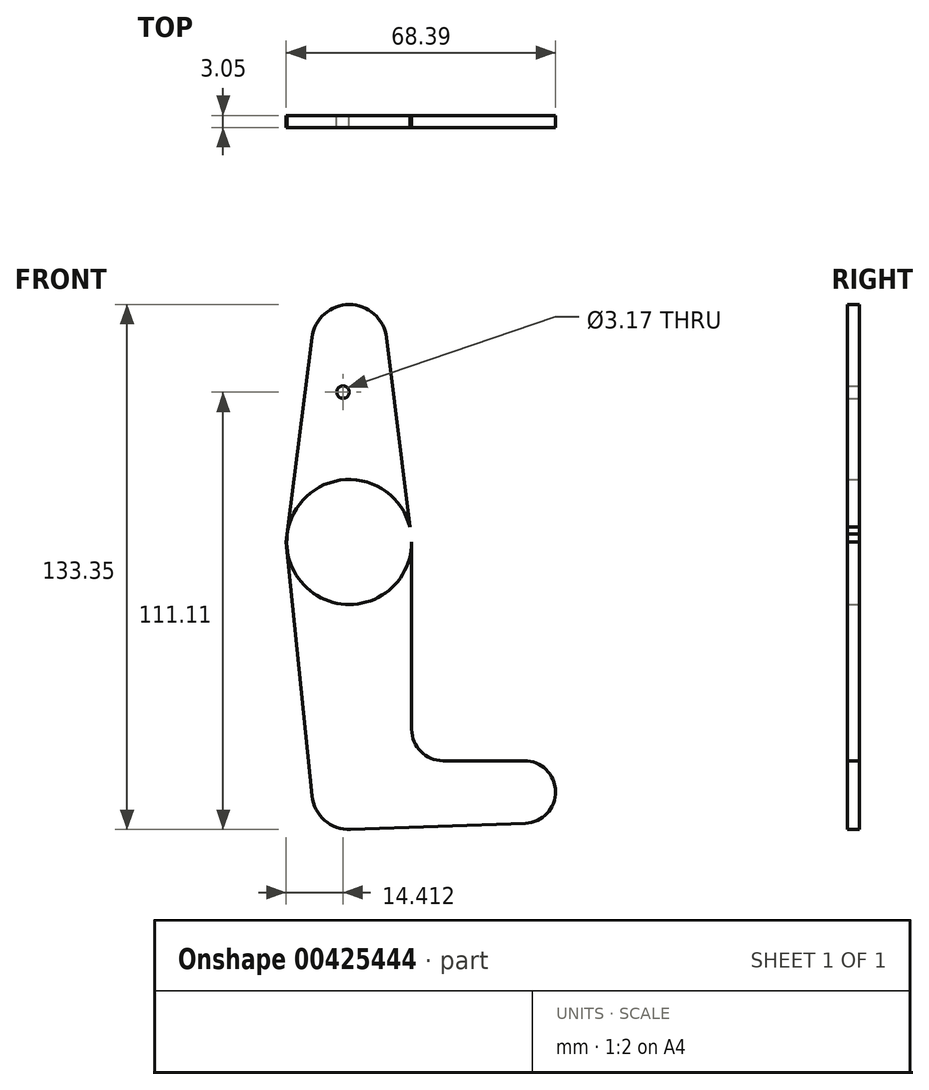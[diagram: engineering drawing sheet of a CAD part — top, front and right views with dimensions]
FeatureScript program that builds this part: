
annotation { "Feature Type Name" : "Feature", "Feature Type Description" : "" }
export const myFeature = defineFeature(function(context is Context, id is Id, definition is map)
    precondition{}
    {
        {
            var Q0;
            Q0=qCreatedBy(makeId("Front.planeOp"),FACE);
            var sketch = newSketch(context, id + "F0", { "sketchPlane" : qUnion([Q0])});
            skLineSegment(sketch, "E0", {"start": v(0, 50.8) * mm, "end": v(0, -63.5) * mm});
            skLineSegment(sketch, "E1", {"start": v(0, -63.5) * mm, "end": v(44.45, -63.5) * mm});
            skCircle(sketch, "E2", {"center": v(0, 50.8) * mm, "radius": 9.52 * mm});
            skCircle(sketch, "E3", {"center": v(0, 0) * mm, "radius": 15.88 * mm});
            skCircle(sketch, "E4", {"center": v(0, -63.5) * mm, "radius": 9.53 * mm});
            skCircle(sketch, "E5", {"center": v(44.45, -63.5) * mm, "radius": 7.94 * mm});
            skLineSegment(sketch, "E6", {"start": v(-9.45, 52) * mm, "end": v(-16, 0) * mm});
            skLineSegment(sketch, "E7", {"start": v(15.88, 0) * mm, "end": v(9.45, 51.97) * mm});
            skLineSegment(sketch, "E8", {"start": v(-16, 0) * mm, "end": v(-9.48, -64.46) * mm});
            skLineSegment(sketch, "E9", {"start": v(15.88, 0) * mm, "end": v(15.88, -47.61) * mm});
            skLineSegment(sketch, "E10", {"start": v(23.83, -55.56) * mm, "end": v(44.45, -55.56) * mm});
            skLineSegment(sketch, "E11", {"start": v(0.34, -73.02) * mm, "end": v(44.73, -71.43) * mm});
            skArc(sketch, "E12.filletArc", {"start": v(15.88, -47.61) * mm, "mid": v(18.2, -53.23) * mm, "end": v(23.83, -55.56) * mm});
            skCircle(sketch, "E13", {"center": v(-1.59, 38.08) * mm, "radius": 1.59 * mm});
            skSolve(sketch);
        }
        {
            var Q0;
            {var subQ5=sQuery(id+"F0.wireOp",EDGE,"E13");Q0=makeQuery(id+"F0.imprint","IMPRINT",FACE,{"disambiguationData":[TD([[makeQuery(id+"F0.imprint","IMPRINT",EDGE,{"derivedFrom":subQ5}),-1.0]])]});}
            var Q1;
            {var subQ3=sQuery(id+"F0.wireOp",EDGE,"E0");var subQ8=makeQuery(id+"F0.imprint","INTERSECT",VERTEX,{"derivedFrom":[subQ3,sQuery(id+"F0.wireOp",EDGE,"E13")]});Q1=makeQuery(id+"F0.imprint","IMPRINT",FACE,{"disambiguationData":[TD([[makeQuery(id+"F0.imprint","IMPRINT",EDGE,{"disambiguationData":[TD([[subQ8,1.0]])],"derivedFrom":subQ3}),1.0]])]});}
            var Q2;
            {var subQ0=sQuery(id+"F0.wireOp",EDGE,"E3");var subQ1=sQuery(id+"F0.wireOp",EDGE,"E0");var subQ2=makeQuery(id+"F0.imprint","INTERSECT",VERTEX,{"disambiguationData":[OD(0.0)],"derivedFrom":[subQ1,subQ0]});Q2=makeQuery(id+"F0.imprint","IMPRINT",FACE,{"disambiguationData":[TD([[makeQuery(id+"F0.imprint","IMPRINT",EDGE,{"disambiguationData":[TD([[subQ2,-1.0]])],"derivedFrom":subQ1}),1.0]])]});}
            var Q3;
            {var subQ0=sQuery(id+"F0.wireOp",EDGE,"E3");var subQ1=sQuery(id+"F0.wireOp",EDGE,"E0");var subQ2=makeQuery(id+"F0.imprint","INTERSECT",VERTEX,{"disambiguationData":[OD(0.0)],"derivedFrom":[subQ1,subQ0]});Q3=makeQuery(id+"F0.imprint","IMPRINT",FACE,{"disambiguationData":[TD([[makeQuery(id+"F0.imprint","IMPRINT",EDGE,{"disambiguationData":[TD([[subQ2,-1.0]])],"derivedFrom":subQ1}),-1.0]])]});}
            var Q4;
            {var subQ5=sQuery(id+"F0.wireOp",EDGE,"E9");Q4=makeQuery(id+"F0.imprint","IMPRINT",FACE,{"disambiguationData":[TD([[makeQuery(id+"F0.imprint","IMPRINT",EDGE,{"derivedFrom":subQ5}),-1.0]])]});}
            var Q5;
            {var subQ0=sQuery(id+"F0.wireOp",EDGE,"E8");Q5=makeQuery(id+"F0.imprint","IMPRINT",FACE,{"disambiguationData":[TD([[makeQuery(id+"F0.imprint","IMPRINT",EDGE,{"derivedFrom":subQ0}),1.0]])]});}
            var Q6;
            {var subQ0=sQuery(id+"F0.wireOp",EDGE,"E1");var subQ1=sQuery(id+"F0.wireOp",EDGE,"E0");var subQ2=makeQuery(id+"F0.imprint","INTERSECT",VERTEX,{"derivedFrom":[subQ1,subQ0]});Q6=makeQuery(id+"F0.imprint","IMPRINT",FACE,{"disambiguationData":[TD([[makeQuery(id+"F0.imprint","IMPRINT",EDGE,{"disambiguationData":[TD([[subQ2,1.0]])],"derivedFrom":subQ1}),1.0]])]});}
            var Q7;
            {var subQ3=sQuery(id+"F0.wireOp",EDGE,"E0");var subQ5=sQuery(id+"F0.wireOp",EDGE,"E1");var subQ6=makeQuery(id+"F0.imprint","INTERSECT",VERTEX,{"derivedFrom":[subQ3,subQ5]});Q7=makeQuery(id+"F0.imprint","IMPRINT",FACE,{"disambiguationData":[TD([[makeQuery(id+"F0.imprint","IMPRINT",EDGE,{"disambiguationData":[TD([[subQ6,1.0]])],"derivedFrom":subQ3}),-1.0]])]});}
            var Q8;
            {var subQ5=sQuery(id+"F0.wireOp",EDGE,"E11");Q8=makeQuery(id+"F0.imprint","IMPRINT",FACE,{"disambiguationData":[TD([[makeQuery(id+"F0.imprint","IMPRINT",EDGE,{"derivedFrom":subQ5}),1.0]])]});}
            var Q9;
            {var subQ0=sQuery(id+"F0.wireOp",EDGE,"E2");var subQ1=makeQuery(id+"F0.imprint","INTERSECT",VERTEX,{"derivedFrom":[subQ0,sQuery(id+"F0.wireOp",EDGE,"E6")]});Q9=makeQuery(id+"F0.imprint","IMPRINT",FACE,{"disambiguationData":[TD([[makeQuery(id+"F0.imprint","IMPRINT",EDGE,{"disambiguationData":[TD([[subQ1,1.0]])],"derivedFrom":subQ0}),1.0]])]});}
            var Q10;
            {var subQ0=sQuery(id+"F0.wireOp",EDGE,"E5");var subQ1=makeQuery(id+"F0.imprint","INTERSECT",VERTEX,{"derivedFrom":[subQ0,sQuery(id+"F0.wireOp",EDGE,"E10")]});Q10=makeQuery(id+"F0.imprint","IMPRINT",FACE,{"disambiguationData":[TD([[makeQuery(id+"F0.imprint","IMPRINT",EDGE,{"disambiguationData":[TD([[subQ1,-1.0]])],"derivedFrom":subQ0}),1.0]])]});}
            extrude(context, id + "F1", {"entities" : qUnion([Q0, Q1, Q2, Q3, Q4, Q5, Q6, Q7, Q8, Q9, Q10]), "depth" : 3.05 * mm});
        }
    });
